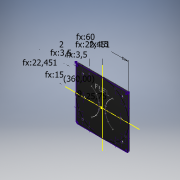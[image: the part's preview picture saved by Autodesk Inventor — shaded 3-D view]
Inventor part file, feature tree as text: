
AUTODESK INVENTOR PART (.ipt)
format: ipt  version: 2019 (Build 230136000, 136)  size: 363,008 bytes
history: native  units: mm
features: hole x3, sketch x2, extrude x2, other x1
ambient origin geometry x8: Origin, YZ Plane, XZ Plane, XY Plane, X Axis, Y Axis, Z Axis, Center Point
bodies: Solid1 (feature_tree)
feature tree (8):
  other  "<userpath>\OneDrive - Van Ierland\Documents\Inventor\FlightSim\Instrument.xlsx"
  sketch  "Sketch1"  dims[d0=60.0mm d1=2.0mm]
  extrude  "Extrusion1"  Depth=2.0mm
  hole  "Hole1"  [1 undecoded]
  hole  "Hole2"  [1 undecoded]
  hole  "Hole3"  [1 undecoded]
  extrude  "Extrusion2"  Depth=3.5mm
  sketch  "Sketch2"  dims[d2=22.45064mm d3=22.45064mm d4=15.0mm d5=15.0mm d6=3.5mm d7=3.5mm d8=40.0mm d10=360.0deg d12=1.5mm d13=0.0mm d14=3.4mm d15=6.0mm d16=6.3mm d17=2.0mm d18=90.0deg d19=8.0mm d20=20.594885mm d21=2.4mm d22=6.0mm d23=4.4mm d24=2.0mm d25=90.0deg d26=8.0mm d27=20.594885mm d28=9.0mm d29=3.4mm d30=6.0mm d31=4.0mm d32=2.0mm d33=90.0deg d34=8.0mm d35=20.594885mm d36=25.75mm d44=0.0mm d47=0.0mm d53=0.1mm d54=0.0mm d69=36.0mm d70=35.0mm d71=120.0deg d72=2.0mm d73=0.5mm d78=18.0mm d79=17.5mm d80=60.0mm d82=120.0deg]
note: 3 required parameter values undecoded (feature->parameter linkage not recoverable at this tier; creation-order binding heuristic only, values carry confidence <= 0.55)
